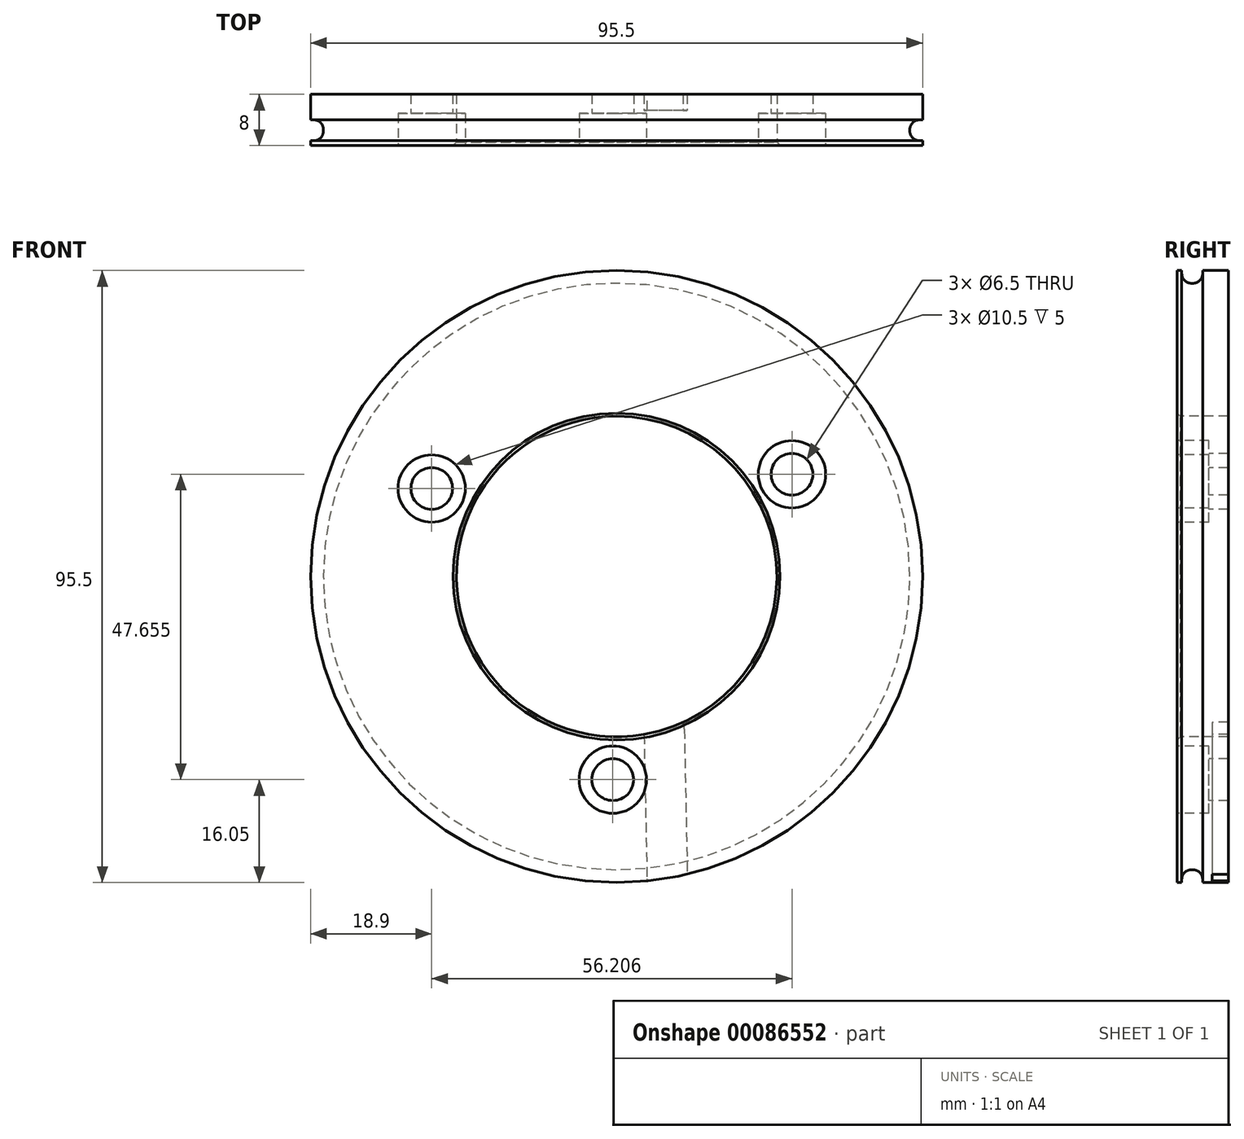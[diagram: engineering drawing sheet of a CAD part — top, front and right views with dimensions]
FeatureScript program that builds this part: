
annotation { "Feature Type Name" : "Feature", "Feature Type Description" : "" }
export const myFeature = defineFeature(function(context is Context, id is Id, definition is map)
    precondition{}
    {
        {
            var Q0;
            Q0=qCreatedBy(makeId("Top.planeOp"),FACE);
            var sketch = newSketch(context, id + "F0", { "sketchPlane" : qUnion([Q0])});
            skLineSegment(sketch, "E0.bottom", {"start": v(-47.75, -8) * mm, "end": v(-25, -8) * mm});
            skLineSegment(sketch, "E0.top", {"start": v(-47.75, 0) * mm, "end": v(-25, 0) * mm});
            skLineSegment(sketch, "E0.right", {"start": v(-25, -8) * mm, "end": v(-25, 0) * mm});
            skLineSegment(sketch, "E1", {"start": v(-47.75, -7.25) * mm, "end": v(-47.25, -7.25) * mm});
            skLineSegment(sketch, "E2", {"start": v(-45.75, -5.75) * mm, "end": v(-45.75, -5.5) * mm});
            skLineSegment(sketch, "E3", {"start": v(-47.25, -4) * mm, "end": v(-47.75, -4) * mm});
            skLineSegment(sketch, "E4", {"start": v(-47.75, -8) * mm, "end": v(-47.75, -7.25) * mm});
            skLineSegment(sketch, "E5", {"start": v(-47.75, -4) * mm, "end": v(-47.75, 0) * mm});
            skPoint(sketch, "E6.visualSharp", {"position": v(-45.75, -7.25) * mm});
            skArc(sketch, "E6.filletArc", {"start": v(-47.25, -7.25) * mm, "mid": v(-46.19, -6.81) * mm, "end": v(-45.75, -5.75) * mm});
            skPoint(sketch, "E7.visualSharp", {"position": v(-45.75, -4) * mm});
            skArc(sketch, "E7.filletArc", {"start": v(-45.75, -5.5) * mm, "mid": v(-46.19, -4.44) * mm, "end": v(-47.25, -4) * mm});
            skLineSegment(sketch, "E8", {"start": v(0, -36.9) * mm, "end": v(0, 45.6) * mm, "construction": true});
            skSolve(sketch);
        }
        {
            var Q0;
            Q0=makeQuery(id+"F0.imprint","IMPRINT",FACE,{"disambiguationData":[TD([[makeQuery(id+"F0.imprint","IMPRINT",EDGE,{"derivedFrom":sQuery(id+"F0.wireOp",EDGE,"E0.bottom")}),1.0]])]});
            var Q1;
            Q1=sQuery(id+"F0.wireOp",EDGE,"E8");
            revolve(context, id + "F1", {"entities" : qUnion([Q0]), "axis" : qUnion([Q1]), "revolveType" : RevolveType.FULL});
        }
        {
            var Q0;
            Q0=makeQuery(id+"F1.opRevolve","SWEPT_EDGE",EDGE,{"disambiguationData":[OSD([sQuery(id+"F0.wireOp",EDGE,"E0.bottom"),sQuery(id+"F0.wireOp",EDGE,"E0.right")])]});
            chamfer(context, id + "F2", {"entities" : qUnion([Q0]), "width" : .5 * mm, "tangentPropagation" : true});
        }
        {
            var Q0;
            Q0=makeQuery(id+"F1.opRevolve","SWEPT_FACE",FACE,{"disambiguationData":[OSD([sQuery(id+"F0.wireOp",EDGE,"E0.top")])]});
            var sketch = newSketch(context, id + "F3", { "sketchPlane" : qUnion([Q0])});
            skLineSegment(sketch, "E9", {"start": v(-7.41, -23.88) * mm, "end": v(-7.89, -47.1) * mm});
            skArc(sketch, "E10.0.startCap", {"start": v(-10.56, -23.81) * mm, "mid": v(-7.35, -20.73) * mm, "end": v(-4.27, -23.94) * mm});
            skArc(sketch, "E10.0.endCap", {"start": v(-4.74, -47.16) * mm, "mid": v(-7.95, -50.24) * mm, "end": v(-11.04, -47.03) * mm});
            skLineSegment(sketch, "E10.0.left", {"start": v(-4.27, -23.94) * mm, "end": v(-4.74, -47.16) * mm});
            skLineSegment(sketch, "E10.0.right", {"start": v(-10.56, -23.81) * mm, "end": v(-11.04, -47.03) * mm});
            skSolve(sketch);
        }
        {
            var Q0;
            Q0=qSketchRegion(id+"F3",true);
            extrude(context, id + "F4", {"entities" : qUnion([Q0]), "operationType" : NewBodyOperationType.REMOVE, "oppositeDirection" : true, "depth" : 2.5 * mm});
        }
        {
            var Q0;
            Q0=makeQuery(id+"F1.opRevolve","SWEPT_FACE",FACE,{"disambiguationData":[OSD([sQuery(id+"F0.wireOp",EDGE,"E0.bottom")])]});
            var sketch = newSketch(context, id + "F5", { "sketchPlane" : qUnion([Q0])});
            skPoint(sketch, "E11", {"position": v(-28.85, 13.73) * mm});
            skPoint(sketch, "E12", {"position": v(27.36, 15.96) * mm});
            skPoint(sketch, "E13", {"position": v(-0.6, -31.7) * mm});
            skSolve(sketch);
        }
        {
            var Q0;
            Q0=sQuery(id+"F5.wireOp",VERTEX,"E11");
            var Q1;
            Q1=sQuery(id+"F5.wireOp",VERTEX,"E12");
            var Q2;
            Q2=sQuery(id+"F5.wireOp",VERTEX,"E13");
            var Q3;
            Q3=makeQuery(id+"F1.opRevolve","SWEPT_BODY",BODY,{"disambiguationData":[OSD([sQuery(id+"F0.wireOp",EDGE,"E0.bottom"),sQuery(id+"F0.wireOp",EDGE,"E0.top"),sQuery(id+"F0.wireOp",EDGE,"E0.right"),sQuery(id+"F0.wireOp",EDGE,"E1"),sQuery(id+"F0.wireOp",EDGE,"E2"),sQuery(id+"F0.wireOp",EDGE,"E3"),sQuery(id+"F0.wireOp",EDGE,"E4"),sQuery(id+"F0.wireOp",EDGE,"E5"),sQuery(id+"F0.wireOp",EDGE,"E6.filletArc"),sQuery(id+"F0.wireOp",EDGE,"E7.filletArc")])]});
            hole(context, id + "F6", {"style" : HoleStyle.C_BORE, "endStyle" : HoleEndStyle.THROUGH, "holeDiameter" : 6.5 * mm, "cBoreDiameter" : 10.5 * mm, "cBoreDepth" : 5 * mm, "locations" : qUnion([Q0, Q1, Q2]), "scope" : qUnion([Q3]), "isTappedThrough" : true});
        }
    });
